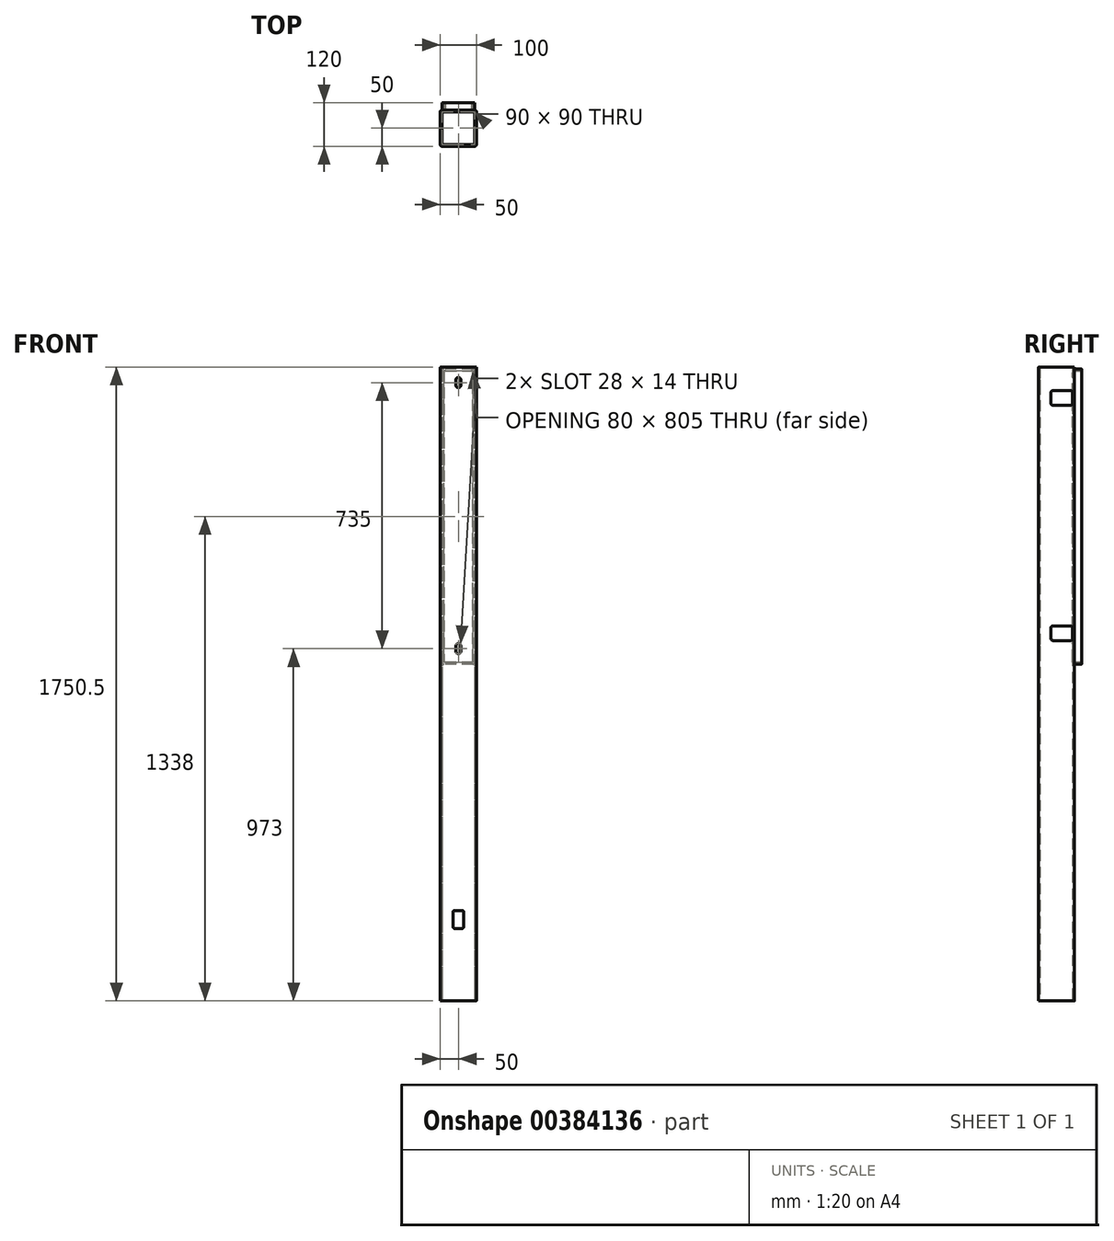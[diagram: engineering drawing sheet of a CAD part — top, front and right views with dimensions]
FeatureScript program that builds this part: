
annotation { "Feature Type Name" : "Feature", "Feature Type Description" : "" }
export const myFeature = defineFeature(function(context is Context, id is Id, definition is map)
    precondition{}
    {
        {
            var Q0;
            Q0=qCreatedBy(makeId("Top.planeOp"),FACE);
            var sketch = newSketch(context, id + "F0", { "sketchPlane" : qUnion([Q0])});
            skLineSegment(sketch, "E0.bottom", {"start": v(45, 50) * mm, "end": v(-45, 50) * mm});
            skLineSegment(sketch, "E0.top", {"start": v(45, -50) * mm, "end": v(-45, -50) * mm});
            skLineSegment(sketch, "E0.left", {"start": v(50, 45) * mm, "end": v(50, -45) * mm});
            skLineSegment(sketch, "E0.right", {"start": v(-50, 45) * mm, "end": v(-50, -45) * mm});
            skPoint(sketch, "E0.middle", {"position": v(0, 0) * mm});
            skPoint(sketch, "E1.visualSharp", {"position": v(-50, 50) * mm});
            skArc(sketch, "E1.filletArc", {"start": v(-45, 50) * mm, "mid": v(-48.54, 48.54) * mm, "end": v(-50, 45) * mm});
            skPoint(sketch, "E2.visualSharp", {"position": v(50, 50) * mm});
            skArc(sketch, "E2.filletArc", {"start": v(50, 45) * mm, "mid": v(48.54, 48.54) * mm, "end": v(45, 50) * mm});
            skPoint(sketch, "E3.visualSharp", {"position": v(-50, -50) * mm});
            skArc(sketch, "E3.filletArc", {"start": v(-50, -45) * mm, "mid": v(-48.54, -48.54) * mm, "end": v(-45, -50) * mm});
            skPoint(sketch, "E4.visualSharp", {"position": v(50, -50) * mm});
            skArc(sketch, "E4.filletArc", {"start": v(45, -50) * mm, "mid": v(48.54, -48.54) * mm, "end": v(50, -45) * mm});
            skLineSegment(sketch, "E5.bottom", {"start": v(45, 45) * mm, "end": v(-45, 45) * mm});
            skLineSegment(sketch, "E5.top", {"start": v(45, -45) * mm, "end": v(-45, -45) * mm});
            skLineSegment(sketch, "E5.left", {"start": v(45, 45) * mm, "end": v(45, -45) * mm});
            skLineSegment(sketch, "E5.right", {"start": v(-45, 45) * mm, "end": v(-45, -45) * mm});
            skSolve(sketch);
        }
        {
            var Q0;
            Q0=makeQuery(id+"F0.imprint","IMPRINT",FACE,{"disambiguationData":[TD([[makeQuery(id+"F0.imprint","IMPRINT",EDGE,{"derivedFrom":sQuery(id+"F0.wireOp",EDGE,"E0.bottom")}),1.0]])]});
            extrude(context, id + "F1", {"entities" : qUnion([Q0]), "depth" : 1750.5 * mm});
        }
        {
            var Q0;
            Q0=makeQuery(id+"F1.opExtrude","SWEPT_FACE",FACE,{"disambiguationData":[OSD([sQuery(id+"F0.wireOp",EDGE,"E0.top")])]});
            var sketch = newSketch(context, id + "F2", { "sketchPlane" : qUnion([Q0])});
            skLineSegment(sketch, "E6.bottom", {"start": v(-10, 200) * mm, "end": v(10, 200) * mm});
            skLineSegment(sketch, "E6.top", {"start": v(-10, 250) * mm, "end": v(10, 250) * mm});
            skLineSegment(sketch, "E6.left", {"start": v(-15, 205) * mm, "end": v(-15, 245) * mm});
            skLineSegment(sketch, "E6.right", {"start": v(15, 205) * mm, "end": v(15, 245) * mm});
            skPoint(sketch, "E6.middle", {"position": v(0, 225) * mm});
            skPoint(sketch, "E7.visualSharp", {"position": v(-15, 250) * mm});
            skArc(sketch, "E7.filletArc", {"start": v(-10, 250) * mm, "mid": v(-13.54, 248.54) * mm, "end": v(-15, 245) * mm});
            skPoint(sketch, "E8.visualSharp", {"position": v(15, 250) * mm});
            skArc(sketch, "E8.filletArc", {"start": v(15, 245) * mm, "mid": v(13.54, 248.54) * mm, "end": v(10, 250) * mm});
            skPoint(sketch, "E9.visualSharp", {"position": v(15, 200) * mm});
            skArc(sketch, "E9.filletArc", {"start": v(10, 200) * mm, "mid": v(13.54, 201.46) * mm, "end": v(15, 205) * mm});
            skPoint(sketch, "E10.visualSharp", {"position": v(-15, 200) * mm});
            skArc(sketch, "E10.filletArc", {"start": v(-15, 205) * mm, "mid": v(-13.54, 201.46) * mm, "end": v(-10, 200) * mm});
            skSolve(sketch);
        }
        {
            var Q0;
            Q0=qSketchRegion(id+"F2",true);
            var Q1;
            Q1=makeQuery(id+"F2.imprint","IMPRINT",FACE,{"disambiguationData":[TD([[makeQuery(id+"F2.imprint","IMPRINT",EDGE,{"derivedFrom":sQuery(id+"F2.wireOp",EDGE,"E6.bottom")}),1.0]])]});
            extrude(context, id + "F3", {"entities" : qUnion([Q0, Q1]), "operationType" : NewBodyOperationType.REMOVE, "oppositeDirection" : true, "depth" : 4 * mm});
        }
        {
            var Q0;
            Q0=makeQuery(id+"F1.opExtrude","SWEPT_FACE",FACE,{"disambiguationData":[OSD([sQuery(id+"F0.wireOp",EDGE,"E0.bottom")])]});
            var sketch = newSketch(context, id + "F4", { "sketchPlane" : qUnion([Q0])});
            skPoint(sketch, "E11", {"position": v(0, 1750.5) * mm});
            skPoint(sketch, "E12", {"position": v(0, 1740.5) * mm});
            skPoint(sketch, "E13", {"position": v(0, 935.5) * mm});
            skPoint(sketch, "E14", {"position": v(-40, 1740.5) * mm});
            skPoint(sketch, "E15", {"position": v(-40, 940.5) * mm});
            skPoint(sketch, "E16", {"position": v(40, 935.5) * mm});
            skPoint(sketch, "E17", {"position": v(40, 1740.5) * mm});
            skLineSegment(sketch, "E18.bottom", {"start": v(-35, 1740.5) * mm, "end": v(35, 1740.5) * mm});
            skLineSegment(sketch, "E18.top", {"start": v(-35, 935.5) * mm, "end": v(35, 935.5) * mm});
            skLineSegment(sketch, "E18.left", {"start": v(-40, 1735.5) * mm, "end": v(-40, 940.5) * mm});
            skLineSegment(sketch, "E18.right", {"start": v(40, 1735.5) * mm, "end": v(40, 940.5) * mm});
            skArc(sketch, "E19.filletArc", {"start": v(-35, 1740.5) * mm, "mid": v(-38.54, 1739.04) * mm, "end": v(-40, 1735.5) * mm});
            skArc(sketch, "E20.filletArc", {"start": v(40, 1735.5) * mm, "mid": v(38.54, 1739.04) * mm, "end": v(35, 1740.5) * mm});
            skArc(sketch, "E21.filletArc", {"start": v(35, 935.5) * mm, "mid": v(38.54, 936.96) * mm, "end": v(40, 940.5) * mm});
            skPoint(sketch, "E22.visualSharp", {"position": v(-40, 935.5) * mm});
            skArc(sketch, "E22.filletArc", {"start": v(-40, 940.5) * mm, "mid": v(-38.54, 936.96) * mm, "end": v(-35, 935.5) * mm});
            skSolve(sketch);
        }
        {
            var Q0;
            Q0=makeQuery(id+"F4.imprint","IMPRINT",FACE,{"disambiguationData":[TD([[makeQuery(id+"F4.imprint","IMPRINT",EDGE,{"derivedFrom":sQuery(id+"F4.wireOp",EDGE,"E18.bottom")}),-1.0]])]});
            extrude(context, id + "F5", {"entities" : qUnion([Q0]), "operationType" : NewBodyOperationType.REMOVE, "oppositeDirection" : true, "depth" : 25 * mm});
        }
        {
            var Q0;
            Q0=makeQuery(id+"F1.opExtrude","SWEPT_FACE",FACE,{"disambiguationData":[OSD([sQuery(id+"F0.wireOp",EDGE,"E0.top")])]});
            var sketch = newSketch(context, id + "F6", { "sketchPlane" : qUnion([Q0])});
            skArc(sketch, "E23", {"start": v(7, 980) * mm, "mid": v(0, 987) * mm, "end": v(-7, 980) * mm});
            skArc(sketch, "E24", {"start": v(-7, 966) * mm, "mid": v(0, 959) * mm, "end": v(7, 966) * mm});
            skLineSegment(sketch, "E25", {"start": v(7, 980) * mm, "end": v(7, 966) * mm});
            skLineSegment(sketch, "E26", {"start": v(-7, 966) * mm, "end": v(-7, 980) * mm});
            skPoint(sketch, "E27.orphan", {"position": v(0, 973) * mm});
            skArc(sketch, "E28", {"start": v(-7, 1701) * mm, "mid": v(0, 1694) * mm, "end": v(7, 1701) * mm});
            skArc(sketch, "E29", {"start": v(7, 1715) * mm, "mid": v(0, 1722) * mm, "end": v(-7, 1715) * mm});
            skPoint(sketch, "E30.center.orphan", {"position": v(0, 1708) * mm});
            skLineSegment(sketch, "E31", {"start": v(7, 1715) * mm, "end": v(7, 1701) * mm});
            skLineSegment(sketch, "E32", {"start": v(-7, 1701) * mm, "end": v(-7, 1715) * mm});
            skSolve(sketch);
        }
        {
            var Q0;
            Q0=makeQuery(id+"F6.imprint","IMPRINT",FACE,{"disambiguationData":[TD([[makeQuery(id+"F6.imprint","IMPRINT",EDGE,{"derivedFrom":sQuery(id+"F6.wireOp",EDGE,"E23")}),1.0]])]});
            var Q1;
            Q1=makeQuery(id+"F6.imprint","IMPRINT",FACE,{"disambiguationData":[TD([[makeQuery(id+"F6.imprint","IMPRINT",EDGE,{"derivedFrom":sQuery(id+"F6.wireOp",EDGE,"E28")}),1.0]])]});
            extrude(context, id + "F7", {"entities" : qUnion([Q0, Q1]), "operationType" : NewBodyOperationType.REMOVE, "oppositeDirection" : true, "depth" : 25 * mm});
        }
        {
            var Q0;
            Q0=makeQuery(id+"F1.opExtrude","SWEPT_FACE",FACE,{"disambiguationData":[OSD([sQuery(id+"F0.wireOp",EDGE,"E0.left")])]});
            var sketch = newSketch(context, id + "F8", { "sketchPlane" : qUnion([Q0])});
            skLineSegment(sketch, "E33.bottom", {"start": v(-10, 1685.5) * mm, "end": v(40, 1685.5) * mm});
            skLineSegment(sketch, "E33.top", {"start": v(-10, 1645.5) * mm, "end": v(40, 1645.5) * mm});
            skLineSegment(sketch, "E33.left", {"start": v(-15, 1680.5) * mm, "end": v(-15, 1650.5) * mm});
            skLineSegment(sketch, "E33.right", {"start": v(45, 1680.5) * mm, "end": v(45, 1650.5) * mm});
            skPoint(sketch, "E34.visualSharp", {"position": v(-15, 1685.5) * mm});
            skArc(sketch, "E34.filletArc", {"start": v(-10, 1685.5) * mm, "mid": v(-13.54, 1684.04) * mm, "end": v(-15, 1680.5) * mm});
            skPoint(sketch, "E35.visualSharp", {"position": v(-15, 1645.5) * mm});
            skArc(sketch, "E35.filletArc", {"start": v(-15, 1650.5) * mm, "mid": v(-13.54, 1646.96) * mm, "end": v(-10, 1645.5) * mm});
            skPoint(sketch, "E36.visualSharp", {"position": v(45, 1645.5) * mm});
            skArc(sketch, "E36.filletArc", {"start": v(40, 1645.5) * mm, "mid": v(43.54, 1646.96) * mm, "end": v(45, 1650.5) * mm});
            skPoint(sketch, "E37.visualSharp", {"position": v(45, 1685.5) * mm});
            skArc(sketch, "E37.filletArc", {"start": v(45, 1680.5) * mm, "mid": v(43.54, 1684.04) * mm, "end": v(40, 1685.5) * mm});
            skPoint(sketch, "E38.0.1.0", {"position": v(-15, 1035.5) * mm});
            skPoint(sketch, "E38.0.1.1", {"position": v(-15, 995.5) * mm});
            skPoint(sketch, "E38.0.1.2", {"position": v(45, 995.5) * mm});
            skPoint(sketch, "E38.0.1.3", {"position": v(45, 1035.5) * mm});
            skArc(sketch, "E38.0.1.4", {"start": v(40, 995.5) * mm, "mid": v(43.54, 996.96) * mm, "end": v(45, 1000.5) * mm});
            skArc(sketch, "E38.0.1.5", {"start": v(-15, 1000.5) * mm, "mid": v(-13.54, 996.96) * mm, "end": v(-10, 995.5) * mm});
            skLineSegment(sketch, "E38.0.1.6", {"start": v(45, 1030.5) * mm, "end": v(45, 1000.5) * mm});
            skLineSegment(sketch, "E38.0.1.7", {"start": v(-15, 1030.5) * mm, "end": v(-15, 1000.5) * mm});
            skLineSegment(sketch, "E38.0.1.8", {"start": v(-10, 995.5) * mm, "end": v(40, 995.5) * mm});
            skLineSegment(sketch, "E38.0.1.9", {"start": v(-10, 1035.5) * mm, "end": v(40, 1035.5) * mm});
            skArc(sketch, "E38.0.1.10", {"start": v(45, 1030.5) * mm, "mid": v(43.54, 1034.04) * mm, "end": v(40, 1035.5) * mm});
            skArc(sketch, "E38.0.1.11", {"start": v(-10, 1035.5) * mm, "mid": v(-13.54, 1034.04) * mm, "end": v(-15, 1030.5) * mm});
            skLineSegment(sketch, "E38.direction1", {"start": v(-15, 1645.5) * mm, "end": v(7.93, 1645.5) * mm, "construction": true});
            skLineSegment(sketch, "E38.direction2", {"start": v(-15, 1645.5) * mm, "end": v(-15, 995.5) * mm, "construction": true});
            skSolve(sketch);
        }
        {
            var Q0;
            Q0=makeQuery(id+"F8.imprint","IMPRINT",FACE,{"disambiguationData":[TD([[makeQuery(id+"F8.imprint","IMPRINT",EDGE,{"derivedFrom":sQuery(id+"F8.wireOp",EDGE,"E38.0.1.4")}),1.0]])]});
            var Q1;
            Q1=makeQuery(id+"F8.imprint","IMPRINT",FACE,{"disambiguationData":[TD([[makeQuery(id+"F8.imprint","IMPRINT",EDGE,{"derivedFrom":sQuery(id+"F8.wireOp",EDGE,"E33.bottom")}),-1.0]])]});
            extrude(context, id + "F9", {"entities" : qUnion([Q0, Q1]), "operationType" : NewBodyOperationType.REMOVE, "oppositeDirection" : true, "depth" : 25 * mm});
        }
        {
            var Q0;
            Q0=makeQuery(id+"F1.opExtrude","SWEPT_FACE",FACE,{"disambiguationData":[OSD([sQuery(id+"F0.wireOp",EDGE,"E0.right")])]});
            var sketch = newSketch(context, id + "F10", { "sketchPlane" : qUnion([Q0])});
            skLineSegment(sketch, "E39.bottom", {"start": v(-40, 1685.5) * mm, "end": v(10, 1685.5) * mm});
            skLineSegment(sketch, "E39.top", {"start": v(-40, 1645.5) * mm, "end": v(10, 1645.5) * mm});
            skLineSegment(sketch, "E39.left", {"start": v(-45, 1680.5) * mm, "end": v(-45, 1650.5) * mm});
            skLineSegment(sketch, "E39.right", {"start": v(15, 1680.5) * mm, "end": v(15, 1650.5) * mm});
            skPoint(sketch, "E40.visualSharp", {"position": v(-45, 1685.5) * mm});
            skArc(sketch, "E40.filletArc", {"start": v(-40, 1685.5) * mm, "mid": v(-43.54, 1684.04) * mm, "end": v(-45, 1680.5) * mm});
            skPoint(sketch, "E41.visualSharp", {"position": v(15, 1685.5) * mm});
            skArc(sketch, "E41.filletArc", {"start": v(15, 1680.5) * mm, "mid": v(13.54, 1684.04) * mm, "end": v(10, 1685.5) * mm});
            skPoint(sketch, "E42.visualSharp", {"position": v(15, 1645.5) * mm});
            skArc(sketch, "E42.filletArc", {"start": v(10, 1645.5) * mm, "mid": v(13.54, 1646.96) * mm, "end": v(15, 1650.5) * mm});
            skPoint(sketch, "E43.visualSharp", {"position": v(-45, 1645.5) * mm});
            skArc(sketch, "E43.filletArc", {"start": v(-45, 1650.5) * mm, "mid": v(-43.54, 1646.96) * mm, "end": v(-40, 1645.5) * mm});
            skPoint(sketch, "E44.0.1.0", {"position": v(-45, 995.5) * mm});
            skPoint(sketch, "E44.0.1.1", {"position": v(15, 995.5) * mm});
            skPoint(sketch, "E44.0.1.2", {"position": v(15, 1035.5) * mm});
            skPoint(sketch, "E44.0.1.3", {"position": v(-45, 1035.5) * mm});
            skLineSegment(sketch, "E44.0.1.4", {"start": v(-40, 1035.5) * mm, "end": v(10, 1035.5) * mm});
            skLineSegment(sketch, "E44.0.1.5", {"start": v(-40, 995.5) * mm, "end": v(10, 995.5) * mm});
            skLineSegment(sketch, "E44.0.1.6", {"start": v(-45, 1030.5) * mm, "end": v(-45, 1000.5) * mm});
            skLineSegment(sketch, "E44.0.1.7", {"start": v(15, 1030.5) * mm, "end": v(15, 1000.5) * mm});
            skArc(sketch, "E44.0.1.8", {"start": v(-45, 1000.5) * mm, "mid": v(-43.54, 996.96) * mm, "end": v(-40, 995.5) * mm});
            skArc(sketch, "E44.0.1.9", {"start": v(10, 995.5) * mm, "mid": v(13.54, 996.96) * mm, "end": v(15, 1000.5) * mm});
            skArc(sketch, "E44.0.1.10", {"start": v(15, 1030.5) * mm, "mid": v(13.54, 1034.04) * mm, "end": v(10, 1035.5) * mm});
            skArc(sketch, "E44.0.1.11", {"start": v(-40, 1035.5) * mm, "mid": v(-43.54, 1034.04) * mm, "end": v(-45, 1030.5) * mm});
            skLineSegment(sketch, "E44.direction1", {"start": v(-45, 1645.5) * mm, "end": v(-30, 1645.5) * mm, "construction": true});
            skLineSegment(sketch, "E44.direction2", {"start": v(-45, 1645.5) * mm, "end": v(-45, 995.5) * mm, "construction": true});
            skSolve(sketch);
        }
        {
            var Q0;
            Q0=makeQuery(id+"F10.imprint","IMPRINT",FACE,{"disambiguationData":[TD([[makeQuery(id+"F10.imprint","IMPRINT",EDGE,{"derivedFrom":sQuery(id+"F10.wireOp",EDGE,"E39.bottom")}),-1.0]])]});
            var Q1;
            Q1=makeQuery(id+"F10.imprint","IMPRINT",FACE,{"disambiguationData":[TD([[makeQuery(id+"F10.imprint","IMPRINT",EDGE,{"derivedFrom":sQuery(id+"F10.wireOp",EDGE,"E44.0.1.4")}),-1.0]])]});
            extrude(context, id + "F11", {"entities" : qUnion([Q0, Q1]), "operationType" : NewBodyOperationType.REMOVE, "oppositeDirection" : true, "depth" : 25 * mm});
        }
        {
            var Q0;
            Q0=makeQuery(id+"F1.opExtrude","SWEPT_FACE",FACE,{"disambiguationData":[OSD([sQuery(id+"F0.wireOp",EDGE,"E0.bottom")])]});
            var sketch = newSketch(context, id + "F12", { "sketchPlane" : qUnion([Q0])});
            skPoint(sketch, "E45", {"position": v(0, 935.5) * mm});
            skPoint(sketch, "E46", {"position": v(0, 930.5) * mm});
            skPoint(sketch, "E47", {"position": v(40, 1317.94) * mm});
            skPoint(sketch, "E48", {"position": v(45, 1322.18) * mm});
            skPoint(sketch, "E49", {"position": v(-5.96, 1740.5) * mm});
            skPoint(sketch, "E50", {"position": v(-7.18, 1745.35) * mm});
            skLineSegment(sketch, "E51.bottom", {"start": v(-40, 930.5) * mm, "end": v(40, 930.5) * mm});
            skLineSegment(sketch, "E51.top", {"start": v(-40, 1745.35) * mm, "end": v(40, 1745.35) * mm});
            skLineSegment(sketch, "E51.left", {"start": v(-45, 935.5) * mm, "end": v(-45, 1740.35) * mm});
            skLineSegment(sketch, "E51.right", {"start": v(45, 935.5) * mm, "end": v(45, 1740.35) * mm});
            skPoint(sketch, "E52.visualSharp", {"position": v(-45, 1745.35) * mm});
            skArc(sketch, "E52.filletArc", {"start": v(-40, 1745.35) * mm, "mid": v(-43.54, 1743.89) * mm, "end": v(-45, 1740.35) * mm});
            skPoint(sketch, "E53.visualSharp", {"position": v(45, 1745.35) * mm});
            skArc(sketch, "E53.filletArc", {"start": v(45, 1740.35) * mm, "mid": v(43.54, 1743.89) * mm, "end": v(40, 1745.35) * mm});
            skPoint(sketch, "E54.visualSharp", {"position": v(45, 930.5) * mm});
            skArc(sketch, "E54.filletArc", {"start": v(40, 930.5) * mm, "mid": v(43.54, 931.96) * mm, "end": v(45, 935.5) * mm});
            skPoint(sketch, "E55.visualSharp", {"position": v(-45, 930.5) * mm});
            skArc(sketch, "E55.filletArc", {"start": v(-45, 935.5) * mm, "mid": v(-43.54, 931.96) * mm, "end": v(-40, 930.5) * mm});
            skLineSegment(sketch, "E56.bottom", {"start": v(-40, 1740.35) * mm, "end": v(40, 1740.35) * mm});
            skLineSegment(sketch, "E56.top", {"start": v(-40, 935.5) * mm, "end": v(40, 935.5) * mm});
            skLineSegment(sketch, "E56.left", {"start": v(-40, 1740.35) * mm, "end": v(-40, 935.5) * mm});
            skLineSegment(sketch, "E56.right", {"start": v(40, 1740.35) * mm, "end": v(40, 935.5) * mm});
            skSolve(sketch);
        }
        {
            var Q0;
            Q0=makeQuery(id+"F12.imprint","IMPRINT",FACE,{"disambiguationData":[TD([[makeQuery(id+"F12.imprint","IMPRINT",EDGE,{"derivedFrom":sQuery(id+"F12.wireOp",EDGE,"E51.bottom")}),1.0]])]});
            extrude(context, id + "F13", {"entities" : qUnion([Q0]), "operationType" : NewBodyOperationType.ADD, "depth" : 20 * mm, "offsetDistance" : 25 * mm});
        }
    });
